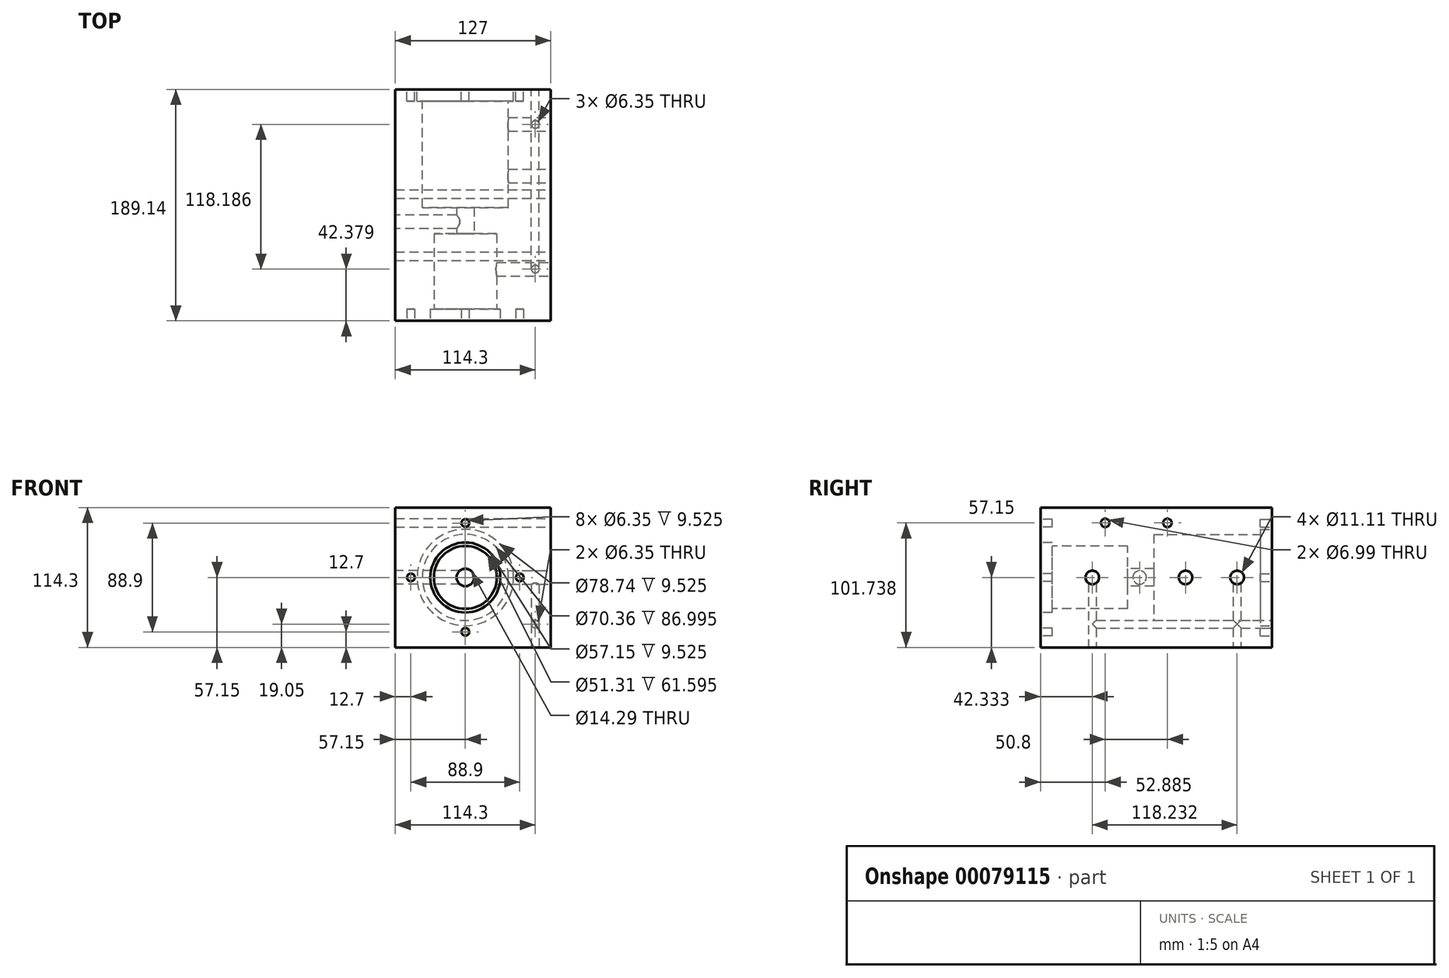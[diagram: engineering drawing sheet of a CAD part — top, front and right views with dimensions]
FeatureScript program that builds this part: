
annotation { "Feature Type Name" : "Feature", "Feature Type Description" : "" }
export const myFeature = defineFeature(function(context is Context, id is Id, definition is map)
    precondition{}
    {
        {
            var Q0;
            Q0=qCreatedBy(makeId("Front.planeOp"),FACE);
            var sketch = newSketch(context, id + "F0", { "sketchPlane" : qUnion([Q0])});
            skLineSegment(sketch, "E0.bottom", {"start": v(57.15, 57.15) * mm, "end": v(-57.15, 57.15) * mm});
            skLineSegment(sketch, "E0.top", {"start": v(57.15, -57.15) * mm, "end": v(-57.15, -57.15) * mm});
            skLineSegment(sketch, "E0.left", {"start": v(57.15, 57.15) * mm, "end": v(57.15, -57.15) * mm});
            skLineSegment(sketch, "E0.right", {"start": v(-57.15, 57.15) * mm, "end": v(-57.15, -57.15) * mm});
            skPoint(sketch, "E0.middle", {"position": v(0, 0) * mm});
            skSolve(sketch);
        }
        {
            var Q0;
            Q0 = qSketchRegion(id + "F0", true);
            extrude(context, id + "F1", {"entities" : qUnion([Q0]), "depth" : 189.14 * mm});
        }
        {
            var Q0;
            Q0=makeQuery(id+"F1.opExtrude","CAP_FACE",FACE,{"disambiguationData":[OSD([sQuery(id+"F0.wireOp",EDGE,"E0.bottom"),sQuery(id+"F0.wireOp",EDGE,"E0.top"),sQuery(id+"F0.wireOp",EDGE,"E0.left"),sQuery(id+"F0.wireOp",EDGE,"E0.right")])],"isStart":true});
            var sketch = newSketch(context, id + "F2", { "sketchPlane" : qUnion([Q0])});
            skCircle(sketch, "E1", {"center": v(0, 0) * mm, "radius": 35.18 * mm});
            skSolve(sketch);
        }
        {
            var Q0;
            Q0 = qSketchRegion(id + "F2", true);
            extrude(context, id + "F3", {"entities" : qUnion([Q0]), "operationType" : NewBodyOperationType.REMOVE, "oppositeDirection" : true, "depth" : 96.52 * mm});
        }
        {
            var Q0;
            Q0=makeQuery(id+"F1.opExtrude","CAP_FACE",FACE,{"disambiguationData":[OSD([sQuery(id+"F0.wireOp",EDGE,"E0.bottom"),sQuery(id+"F0.wireOp",EDGE,"E0.top"),sQuery(id+"F0.wireOp",EDGE,"E0.left"),sQuery(id+"F0.wireOp",EDGE,"E0.right")])],"isStart":true});
            var sketch = newSketch(context, id + "F4", { "sketchPlane" : qUnion([Q0])});
            skCircle(sketch, "E2", {"center": v(0, 0) * mm, "radius": 39.37 * mm});
            skSolve(sketch);
        }
        {
            var Q0;
            Q0 = qSketchRegion(id + "F4", true);
            extrude(context, id + "F5", {"entities" : qUnion([Q0]), "operationType" : NewBodyOperationType.REMOVE, "oppositeDirection" : true, "depth" : 9.52 * mm});
        }
        {
            var Q0;
            Q0=makeQuery(id+"F1.opExtrude","CAP_FACE",FACE,{"disambiguationData":[OSD([sQuery(id+"F0.wireOp",EDGE,"E0.bottom"),sQuery(id+"F0.wireOp",EDGE,"E0.top"),sQuery(id+"F0.wireOp",EDGE,"E0.left"),sQuery(id+"F0.wireOp",EDGE,"E0.right")])],"isStart":false});
            var sketch = newSketch(context, id + "F6", { "sketchPlane" : qUnion([Q0])});
            skCircle(sketch, "E3", {"center": v(0, 0) * mm, "radius": 25.65 * mm});
            skSolve(sketch);
        }
        {
            var Q0;
            Q0 = qSketchRegion(id + "F6", true);
            extrude(context, id + "F7", {"entities" : qUnion([Q0]), "operationType" : NewBodyOperationType.REMOVE, "oppositeDirection" : true, "depth" : 71.12 * mm});
        }
        {
            var Q0;
            Q0=makeQuery(id+"F1.opExtrude","CAP_FACE",FACE,{"disambiguationData":[OSD([sQuery(id+"F0.wireOp",EDGE,"E0.bottom"),sQuery(id+"F0.wireOp",EDGE,"E0.top"),sQuery(id+"F0.wireOp",EDGE,"E0.left"),sQuery(id+"F0.wireOp",EDGE,"E0.right")])],"isStart":false});
            var sketch = newSketch(context, id + "F8", { "sketchPlane" : qUnion([Q0])});
            skCircle(sketch, "E4", {"center": v(0, 0) * mm, "radius": 28.58 * mm});
            skSolve(sketch);
        }
        {
            var Q0;
            Q0 = qSketchRegion(id + "F8", true);
            extrude(context, id + "F9", {"entities" : qUnion([Q0]), "operationType" : NewBodyOperationType.REMOVE, "oppositeDirection" : true, "depth" : 9.52 * mm});
        }
        {
            var Q0;
            Q0=makeQuery(id+"F7.boolean.opBoolean","COPY",FACE,{"derivedFrom":makeQuery(id+"F7.opExtrude","CAP_FACE",FACE,{"disambiguationData":[OSD([sQuery(id+"F6.wireOp",EDGE,"E3")])],"isStart":false})});
            var sketch = newSketch(context, id + "F10", { "sketchPlane" : qUnion([Q0])});
            skCircle(sketch, "E5", {"center": v(0, 0) * mm, "radius": 7.14 * mm});
            skSolve(sketch);
        }
        {
            var Q0;
            Q0 = qSketchRegion(id + "F10", true);
            extrude(context, id + "F11", {"entities" : qUnion([Q0]), "operationType" : NewBodyOperationType.REMOVE, "endBound" : BoundingType.THROUGH_ALL, "oppositeDirection" : true, "depth" : 25.4 * mm});
        }
        {
            var Q0;
            Q0=makeQuery(id+"F1.opExtrude","SWEPT_FACE",FACE,{"disambiguationData":[OSD([sQuery(id+"F0.wireOp",EDGE,"E0.left")])]});
            var sketch = newSketch(context, id + "F12", { "sketchPlane" : qUnion([Q0])});
            skCircle(sketch, "E6", {"center": v(-146.8, 0) * mm, "radius": 5.56 * mm});
            skCircle(sketch, "E7", {"center": v(-70.7, 0) * mm, "radius": 5.56 * mm});
            skCircle(sketch, "E8", {"center": v(-28.58, 0) * mm, "radius": 5.56 * mm});
            skPoint(sketch, "E8.centerSnap0", {"position": v(0, 0) * mm});
            skSolve(sketch);
        }
        {
            var Q0;
            Q0 = qSketchRegion(id + "F12", true);
            extrude(context, id + "F13", {"entities" : qUnion([Q0]), "operationType" : NewBodyOperationType.REMOVE, "endBound" : BoundingType.UP_TO_NEXT, "oppositeDirection" : true, "depth" : 25.4 * mm});
        }
        {
            var Q0;
            Q0=makeQuery(id+"F1.opExtrude","SWEPT_FACE",FACE,{"disambiguationData":[OSD([sQuery(id+"F0.wireOp",EDGE,"E0.right")])]});
            var sketch = newSketch(context, id + "F14", { "sketchPlane" : qUnion([Q0])});
            skCircle(sketch, "E9", {"center": v(108.18, 0) * mm, "radius": 5.56 * mm});
            skPoint(sketch, "E9.centerSnap0", {"position": v(189.14, 0) * mm});
            skSolve(sketch);
        }
        {
            var Q0;
            Q0 = qSketchRegion(id + "F14", true);
            extrude(context, id + "F15", {"entities" : qUnion([Q0]), "operationType" : NewBodyOperationType.REMOVE, "endBound" : BoundingType.UP_TO_NEXT, "oppositeDirection" : true, "depth" : 25.4 * mm});
        }
        {
            var Q0;
            Q0=makeQuery(id+"F1.opExtrude","SWEPT_FACE",FACE,{"disambiguationData":[OSD([sQuery(id+"F0.wireOp",EDGE,"E0.left")])]});
            extrude(context, id + "F16", {"entities" : qUnion([Q0]), "operationType" : NewBodyOperationType.ADD, "depth" : 12.7 * mm});
        }
        {
            var Q0;
            {var subQ0=sQuery(id+"F0.wireOp",EDGE,"E0.left");Q0=makeQuery(id+"F16.boolean.opBoolean","MERGE",FACE,{"derivedFrom":[makeQuery(id+"F1.opExtrude","CAP_FACE",FACE,{"disambiguationData":[OSD([sQuery(id+"F0.wireOp",EDGE,"E0.bottom"),sQuery(id+"F0.wireOp",EDGE,"E0.top"),subQ0,sQuery(id+"F0.wireOp",EDGE,"E0.right")])],"isStart":true}),makeQuery(id+"F16.opExtrude","SWEPT_FACE",FACE,{"disambiguationData":[OSD([subQ0]),TDD([makeQuery(id+"F1.opExtrude","CAP_EDGE",EDGE,{"disambiguationData":[OSD([subQ0])],"isStart":true})])]})]});}
            var sketch = newSketch(context, id + "F17", { "sketchPlane" : qUnion([Q0])});
            skSolve(sketch);
        }
        {
            var Q0;
            {var subQ0=sQuery(id+"F0.wireOp",EDGE,"E0.top");Q0=makeQuery(id+"F16.boolean.opBoolean","MERGE",FACE,{"derivedFrom":[makeQuery(id+"F1.opExtrude","SWEPT_FACE",FACE,{"disambiguationData":[OSD([subQ0])]}),makeQuery(id+"F16.opExtrude","SWEPT_FACE",FACE,{"disambiguationData":[OSD([subQ0,sQuery(id+"F0.wireOp",EDGE,"E0.left")])]})]});}
            var sketch = newSketch(context, id + "F18", { "sketchPlane" : qUnion([Q0])});
            skCircle(sketch, "E10", {"center": v(57.15, 146.76) * mm, "radius": 3.18 * mm});
            skCircle(sketch, "E11", {"center": v(57.15, 28.58) * mm, "radius": 3.18 * mm});
            skSolve(sketch);
        }
        {
            var Q0;
            Q0=makeQuery(id+"F17.imprint","IMPRINT",FACE,{"disambiguationData":[TD([[makeQuery(id+"F17.imprint","IMPRINT",EDGE,{"derivedFrom":makeQuery(id+"F1.opExtrude","CAP_EDGE",EDGE,{"disambiguationData":[OSD([sQuery(id+"F0.wireOp",EDGE,"E0.right")])],"isStart":true})}),-1.0]])]});
            var sketch = newSketch(context, id + "F19", { "sketchPlane" : qUnion([Q0])});
            skCircle(sketch, "E12", {"center": v(-57.15, -38.1) * mm, "radius": 3.18 * mm});
            skSolve(sketch);
        }
        {
            var Q0;
            Q0 = qSketchRegion(id + "F18", true);
            extrude(context, id + "F20", {"entities" : qUnion([Q0]), "operationType" : NewBodyOperationType.REMOVE, "endBound" : BoundingType.UP_TO_NEXT, "oppositeDirection" : true, "depth" : 25.4 * mm});
        }
        {
            var Q0;
            Q0 = qSketchRegion(id + "F19", true);
            extrude(context, id + "F21", {"entities" : qUnion([Q0]), "operationType" : NewBodyOperationType.REMOVE, "oppositeDirection" : true, "depth" : 146.76 * mm});
        }
        {
            var Q0;
            Q0=makeQuery(id+"F16.opExtrude","CAP_FACE",FACE,{"disambiguationData":[OSD([sQuery(id+"F0.wireOp",EDGE,"E0.left")])],"isStart":false});
            var sketch = newSketch(context, id + "F22", { "sketchPlane" : qUnion([Q0])});
            skSolve(sketch);
        }
        {
            var Q0;
            Q0=makeQuery(id+"F0.imprint","IMPRINT",FACE,{"disambiguationData":[TD([[makeQuery(id+"F0.imprint","IMPRINT",EDGE,{"derivedFrom":sQuery(id+"F0.wireOp",EDGE,"E0.bottom")}),1.0]])]});
            var sketch = newSketch(context, id + "F23", { "sketchPlane" : qUnion([Q0])});
            skPoint(sketch, "E13.middle", {"position": v(0, 0) * mm});
            skLineSegment(sketch, "E14", {"start": v(0, 0) * mm, "end": v(-62.61, 0) * mm});
            skPoint(sketch, "E14.endSnap0", {"position": v(-44.45, 0) * mm});
            skLineSegment(sketch, "E15", {"start": v(50.7, 0) * mm, "end": v(37.08, 0) * mm});
            skPoint(sketch, "E15.startSnap0", {"position": v(44.45, 0) * mm});
            skPoint(sketch, "E15.endSnap0", {"position": v(44.45, 0) * mm});
            skLineSegment(sketch, "E16", {"start": v(0, -52.16) * mm, "end": v(0, -30.76) * mm});
            skPoint(sketch, "E16.startSnap0", {"position": v(0, -44.45) * mm});
            skLineSegment(sketch, "E17", {"start": v(0, 40) * mm, "end": v(0, 51.18) * mm});
            skPoint(sketch, "E17.startSnap0", {"position": v(0, 44.45) * mm});
            skCircle(sketch, "E18", {"center": v(0, 44.45) * mm, "radius": 3.18 * mm});
            skCircle(sketch, "E19", {"center": v(44.45, 0) * mm, "radius": 3.18 * mm});
            skCircle(sketch, "E20", {"center": v(-44.45, 0) * mm, "radius": 3.18 * mm});
            skCircle(sketch, "E21", {"center": v(0, -44.45) * mm, "radius": 3.18 * mm});
            skSolve(sketch);
        }
        {
            var Q0;
            Q0 = qSketchRegion(id + "F23", true);
            extrude(context, id + "F24", {"entities" : qUnion([Q0]), "operationType" : NewBodyOperationType.REMOVE, "depth" : 9.52 * mm});
        }
        {
            var Q0;
            {var subQ0=sQuery(id+"F0.wireOp",EDGE,"E0.left");Q0=makeQuery(id+"F16.boolean.opBoolean","MERGE",FACE,{"derivedFrom":[makeQuery(id+"F1.opExtrude","CAP_FACE",FACE,{"disambiguationData":[OSD([sQuery(id+"F0.wireOp",EDGE,"E0.bottom"),sQuery(id+"F0.wireOp",EDGE,"E0.top"),subQ0,sQuery(id+"F0.wireOp",EDGE,"E0.right")])],"isStart":false}),makeQuery(id+"F16.opExtrude","SWEPT_FACE",FACE,{"disambiguationData":[OSD([subQ0]),TDD([makeQuery(id+"F1.opExtrude","CAP_EDGE",EDGE,{"disambiguationData":[OSD([subQ0])],"isStart":false})])]})]});}
            var sketch = newSketch(context, id + "F25", { "sketchPlane" : qUnion([Q0])});
            skPoint(sketch, "E22.middle", {"position": v(0, 0) * mm});
            skCircle(sketch, "E23", {"center": v(-44.45, 0) * mm, "radius": 3.18 * mm});
            skCircle(sketch, "E24", {"center": v(0, 44.45) * mm, "radius": 3.18 * mm});
            skCircle(sketch, "E25", {"center": v(44.45, 0) * mm, "radius": 3.18 * mm});
            skCircle(sketch, "E26", {"center": v(0, -44.45) * mm, "radius": 3.18 * mm});
            skSolve(sketch);
        }
        {
            var Q0;
            Q0 = qSketchRegion(id + "F25", true);
            extrude(context, id + "F26", {"entities" : qUnion([Q0]), "operationType" : NewBodyOperationType.REMOVE, "oppositeDirection" : true, "depth" : 9.52 * mm});
        }
        {
            var Q0;
            Q0=makeQuery(id+"F22.imprint","IMPRINT",FACE,{"disambiguationData":[TD([[makeQuery(id+"F22.imprint","IMPRINT",EDGE,{"derivedFrom":makeQuery(id+"F16.opExtrude","CAP_EDGE",EDGE,{"disambiguationData":[OSD([sQuery(id+"F12.wireOp",EDGE,"E6")])],"isStart":false})}),-1.0]])]});
            var sketch = newSketch(context, id + "F27", { "sketchPlane" : qUnion([Q0])});
            skLineSegment(sketch, "E27", {"start": v(0, 57.29) * mm, "end": v(0, 44.59) * mm});
            skCircle(sketch, "E28", {"center": v(-136.26, 44.59) * mm, "radius": 3.5 * mm});
            skCircle(sketch, "E29", {"center": v(-85.46, 44.59) * mm, "radius": 3.5 * mm});
            skSolve(sketch);
        }
        {
            var Q0;
            Q0 = qSketchRegion(id + "F27", true);
            extrude(context, id + "F28", {"entities" : qUnion([Q0]), "operationType" : NewBodyOperationType.REMOVE, "endBound" : BoundingType.THROUGH_ALL, "oppositeDirection" : true, "depth" : 25.4 * mm});
        }
    });
